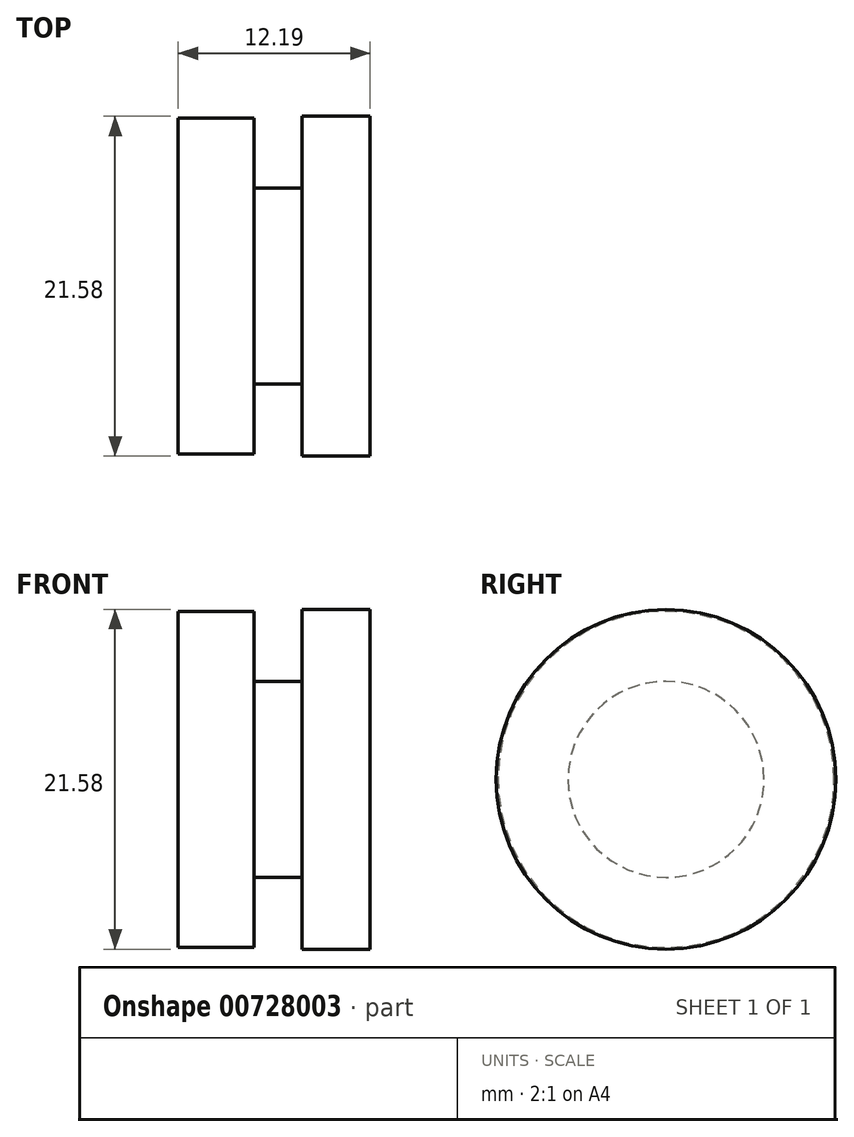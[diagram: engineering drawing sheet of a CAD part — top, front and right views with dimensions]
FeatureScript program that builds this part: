
annotation { "Feature Type Name" : "Feature", "Feature Type Description" : "" }
export const myFeature = defineFeature(function(context is Context, id is Id, definition is map)
    precondition{}
    {
        {
            var Q0;
            Q0=qCreatedBy(makeId("Right.planeOp"),FACE);
            var sketch = newSketch(context, id + "F0", { "sketchPlane" : qUnion([Q0])});
            skCircle(sketch, "E0", {"center": v(0, 0) * mm, "radius": 10.79 * mm});
            skSolve(sketch);
        }
        {
            var Q0;
            Q0=makeQuery(id+"F0.imprint","IMPRINT",FACE,{"disambiguationData":[TD([[makeQuery(id+"F0.imprint","IMPRINT",EDGE,{"derivedFrom":sQuery(id+"F0.wireOp",EDGE,"E0")}),1.0]])]});
            extrude(context, id + "F1", {"entities" : qUnion([Q0]), "depth" : 4.32 * mm, "offsetDistance" : 25.4 * mm});
        }
        {
            var Q0;
            Q0=makeQuery(id+"F1.opExtrude","CAP_FACE",FACE,{"disambiguationData":[OSD([sQuery(id+"F0.wireOp",EDGE,"E0")])],"isStart":true});
            var sketch = newSketch(context, id + "F2", { "sketchPlane" : qUnion([Q0])});
            skCircle(sketch, "E1", {"center": v(0, 0) * mm, "radius": 6.23 * mm});
            skSolve(sketch);
        }
        {
            var Q0;
            Q0=makeQuery(id+"F2.imprint","IMPRINT",FACE,{"disambiguationData":[TD([[makeQuery(id+"F2.imprint","IMPRINT",EDGE,{"derivedFrom":sQuery(id+"F2.wireOp",EDGE,"E1")}),1.0]])]});
            extrude(context, id + "F3", {"entities" : qUnion([Q0]), "operationType" : NewBodyOperationType.ADD, "depth" : 3.05 * mm, "offsetDistance" : 25.4 * mm});
        }
        {
            var Q0;
            Q0=makeQuery(id+"F3.opExtrude","CAP_FACE",FACE,{"disambiguationData":[OSD([sQuery(id+"F2.wireOp",EDGE,"E1")])],"isStart":false});
            var sketch = newSketch(context, id + "F4", { "sketchPlane" : qUnion([Q0])});
            skCircle(sketch, "E2", {"center": v(0, 0) * mm, "radius": 10.68 * mm});
            skSolve(sketch);
        }
        {
            var Q0;
            Q0=makeQuery(id+"F4.imprint","IMPRINT",FACE,{"disambiguationData":[TD([[makeQuery(id+"F4.imprint","IMPRINT",EDGE,{"derivedFrom":makeQuery(id+"F3.opExtrude","CAP_EDGE",EDGE,{"disambiguationData":[OSD([sQuery(id+"F2.wireOp",EDGE,"E1")])],"isStart":false})}),1.0]])]});
            var Q1;
            Q1=makeQuery(id+"F4.imprint","IMPRINT",FACE,{"disambiguationData":[TD([[makeQuery(id+"F4.imprint","IMPRINT",EDGE,{"derivedFrom":sQuery(id+"F4.wireOp",EDGE,"E2")}),1.0]])]});
            extrude(context, id + "F5", {"entities" : qUnion([Q0, Q1]), "operationType" : NewBodyOperationType.ADD, "depth" : 4.83 * mm, "offsetDistance" : 25.4 * mm});
        }
    });
